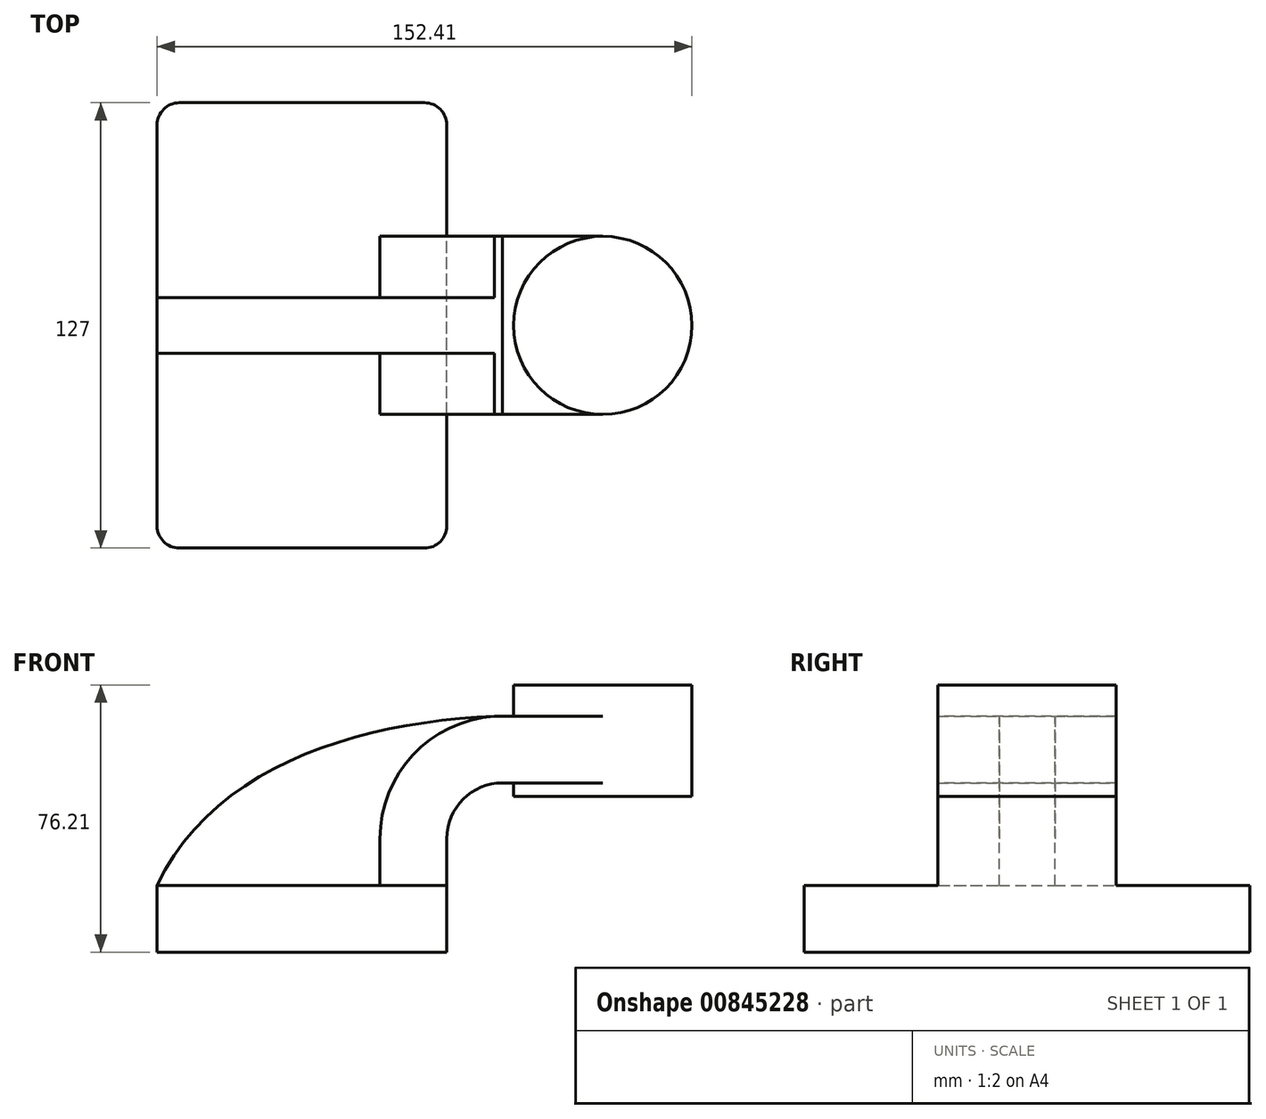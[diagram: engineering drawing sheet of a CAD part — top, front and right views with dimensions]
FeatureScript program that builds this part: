
annotation { "Feature Type Name" : "Feature", "Feature Type Description" : "" }
export const myFeature = defineFeature(function(context is Context, id is Id, definition is map)
    precondition{}
    {
        {
            var Q0;
            Q0=qCreatedBy(makeId("Front.planeOp"),FACE);
            var sketch = newSketch(context, id + "F0", { "sketchPlane" : qUnion([Q0])});
            skLineSegment(sketch, "E0.bottom", {"start": v(-41.28, 9.53) * mm, "end": v(41.28, 9.53) * mm});
            skLineSegment(sketch, "E0.top", {"start": v(-41.27, -9.52) * mm, "end": v(41.28, -9.52) * mm});
            skLineSegment(sketch, "E0.left", {"start": v(-41.28, 9.52) * mm, "end": v(-41.28, -9.53) * mm});
            skLineSegment(sketch, "E0.right", {"start": v(41.28, 9.53) * mm, "end": v(41.28, -9.52) * mm});
            skPoint(sketch, "E0.middle", {"position": v(0, 0) * mm});
            skLineSegment(sketch, "E1.bottom", {"start": v(60.32, 66.68) * mm, "end": v(111.12, 66.68) * mm});
            skLineSegment(sketch, "E1.top", {"start": v(60.32, 34.93) * mm, "end": v(111.12, 34.93) * mm});
            skLineSegment(sketch, "E1.left", {"start": v(60.32, 66.68) * mm, "end": v(60.32, 34.93) * mm});
            skLineSegment(sketch, "E1.right", {"start": v(111.12, 66.68) * mm, "end": v(111.12, 34.93) * mm});
            skPoint(sketch, "E1.middle", {"position": v(85.73, 50.8) * mm});
            skLineSegment(sketch, "E2", {"start": v(41.27, 9.53) * mm, "end": v(41.27, 22.85) * mm});
            skArc(sketch, "E3", {"start": v(41.27, 22.85) * mm, "mid": v(45.92, 34.08) * mm, "end": v(57.15, 38.73) * mm});
            skLineSegment(sketch, "E4", {"start": v(57.15, 38.73) * mm, "end": v(85.73, 38.73) * mm});
            skLineSegment(sketch, "E5.0", {"start": v(57.15, 57.78) * mm, "end": v(85.72, 57.78) * mm});
            skArc(sketch, "E5.1", {"start": v(22.22, 22.85) * mm, "mid": v(32.45, 47.55) * mm, "end": v(57.15, 57.78) * mm});
            skLineSegment(sketch, "E5.2", {"start": v(22.22, 9.53) * mm, "end": v(22.22, 22.85) * mm});
            skFitSpline(sketch, "E6", {"points": [v(-41.28, 9.53) * mm, v(57.15, 57.78) * mm], "startDerivative": vector(49.49, 105.19) * mm, "endDerivative": vector(115.3, 3.2) * mm});
            skLineSegment(sketch, "E7", {"start": v(85.72, 66.68) * mm, "end": v(85.73, 34.93) * mm});
            skSolve(sketch);
        }
        {
            var Q0;
            Q0=makeQuery(id+"F0.imprint","IMPRINT",FACE,{"disambiguationData":[TD([[makeQuery(id+"F0.imprint","IMPRINT",EDGE,{"derivedFrom":sQuery(id+"F0.wireOp",EDGE,"E0.top")}),1.0]])]});
            extrude(context, id + "F1", {"entities" : qUnion([Q0]), "endBound" : BoundingType.SYMMETRIC, "depth" : 127 * mm, "offsetDistance" : 25.4 * mm});
        }
        {
            var Q0;
            {var subQ1=sQuery(id+"F0.wireOp",EDGE,"E2");Q0=makeQuery(id+"F0.imprint","IMPRINT",FACE,{"disambiguationData":[TD([[makeQuery(id+"F0.imprint","IMPRINT",EDGE,{"derivedFrom":subQ1}),1.0]])]});}
            var Q1;
            {var subQ0=sQuery(id+"F0.wireOp",EDGE,"E5.0");var subQ1=sQuery(id+"F0.wireOp",EDGE,"E1.left");var subQ2=makeQuery(id+"F0.imprint","INTERSECT",VERTEX,{"derivedFrom":[subQ1,subQ0]});Q1=makeQuery(id+"F0.imprint","IMPRINT",FACE,{"disambiguationData":[TD([[makeQuery(id+"F0.imprint","IMPRINT",EDGE,{"disambiguationData":[TD([[subQ2,-1.0]])],"derivedFrom":subQ1}),1.0]])]});}
            extrude(context, id + "F2", {"entities" : qUnion([Q0, Q1]), "operationType" : NewBodyOperationType.ADD, "endBound" : BoundingType.SYMMETRIC, "depth" : 50.8 * mm, "offsetDistance" : 25.4 * mm});
        }
        {
            var Q0;
            {var subQ0=sQuery(id+"F0.wireOp",EDGE,"E1.right");Q0=makeQuery(id+"F0.imprint","IMPRINT",FACE,{"disambiguationData":[TD([[makeQuery(id+"F0.imprint","IMPRINT",EDGE,{"derivedFrom":subQ0}),-1.0]])]});}
            var Q1;
            Q1=sQuery(id+"F0.wireOp",EDGE,"E7");
            revolve(context, id + "F3", {"operationType" : NewBodyOperationType.ADD, "surfaceOperationType" : NewSurfaceOperationType.NEW, "entities" : qUnion([Q0]), "axis" : qUnion([Q1]), "revolveType" : RevolveType.FULL});
        }
        {
            var Q0;
            {var subQ3=sQuery(id+"F0.wireOp",EDGE,"E5.2");Q0=makeQuery(id+"F0.imprint","IMPRINT",FACE,{"disambiguationData":[TD([[makeQuery(id+"F0.imprint","IMPRINT",EDGE,{"derivedFrom":subQ3}),1.0]])]});}
            extrude(context, id + "F4", {"entities" : qUnion([Q0]), "operationType" : NewBodyOperationType.ADD, "endBound" : BoundingType.SYMMETRIC, "depth" : 15.88 * mm, "offsetDistance" : 25.4 * mm});
        }
        {
            var Q0;
            Q0=makeQuery(id+"F1.opExtrude","CAP_EDGE",EDGE,{"disambiguationData":[OSD([sQuery(id+"F0.wireOp",EDGE,"E0.right")])],"isStart":true});
            var Q1;
            Q1=makeQuery(id+"F1.opExtrude","CAP_EDGE",EDGE,{"disambiguationData":[OSD([sQuery(id+"F0.wireOp",EDGE,"E0.left")])],"isStart":true});
            var Q2;
            Q2=makeQuery(id+"F1.opExtrude","CAP_EDGE",EDGE,{"disambiguationData":[OSD([sQuery(id+"F0.wireOp",EDGE,"E0.right")])],"isStart":false});
            var Q3;
            Q3=makeQuery(id+"F1.opExtrude","CAP_EDGE",EDGE,{"disambiguationData":[OSD([sQuery(id+"F0.wireOp",EDGE,"E0.left")])],"isStart":false});
            fillet(context, id + "F5", {"entities" : qUnion([Q0, Q1, Q2, Q3]), "radius" : 6.35 * mm, "tangentPropagation" : true, "allowEdgeOverflow" : false});
        }
    });
